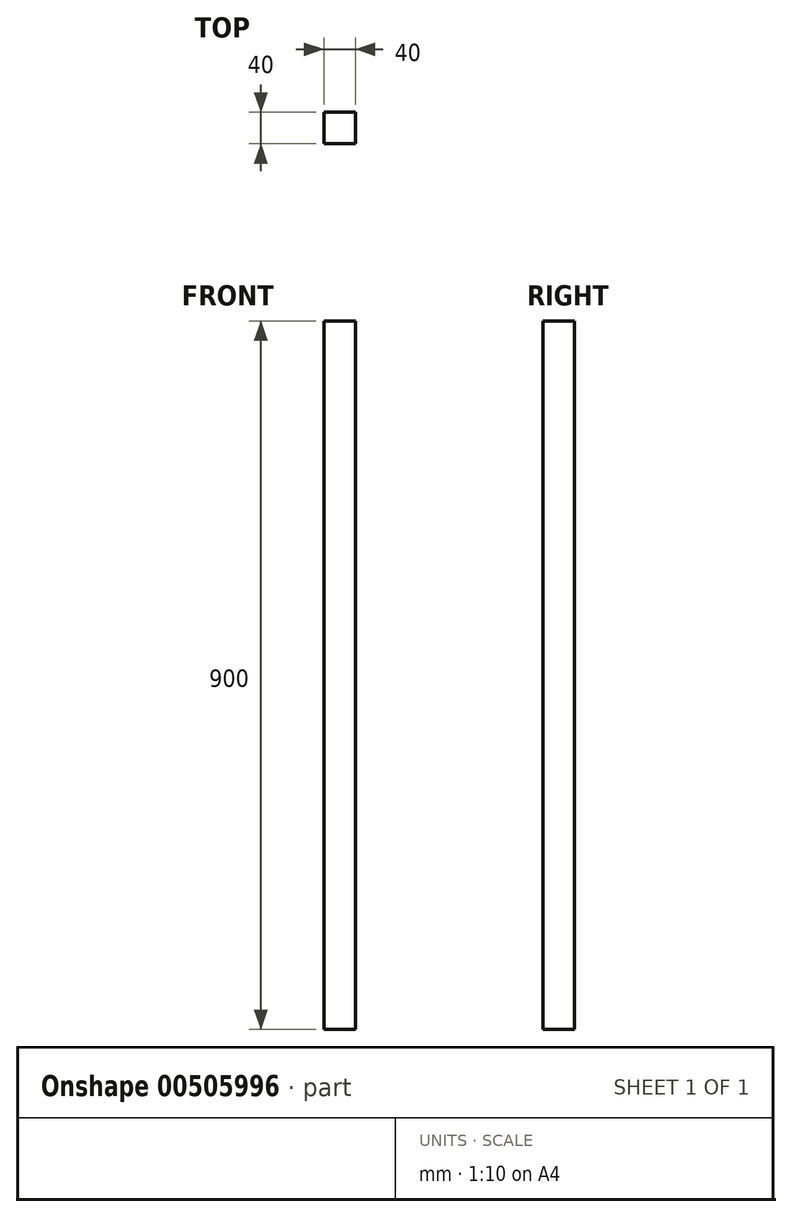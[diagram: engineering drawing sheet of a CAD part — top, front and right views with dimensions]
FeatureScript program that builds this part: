
annotation { "Feature Type Name" : "Feature", "Feature Type Description" : "" }
export const myFeature = defineFeature(function(context is Context, id is Id, definition is map)
    precondition{}
    {
        {
            var Q0;
            Q0=qCreatedBy(makeId("Top.planeOp"),FACE);
            var sketch = newSketch(context, id + "F0", { "sketchPlane" : qUnion([Q0])});
            skLineSegment(sketch, "E0.bottom", {"start": v(0, 0) * mm, "end": v(40, 0) * mm});
            skLineSegment(sketch, "E0.top", {"start": v(0, 40) * mm, "end": v(40, 40) * mm});
            skLineSegment(sketch, "E0.left", {"start": v(0, 0) * mm, "end": v(0, 40) * mm});
            skLineSegment(sketch, "E0.right", {"start": v(40, 0) * mm, "end": v(40, 40) * mm});
            skSolve(sketch);
        }
        {
            var Q0;
            Q0=makeQuery(id+"F0.imprint","IMPRINT",FACE,{"disambiguationData":[TD([[makeQuery(id+"F0.imprint","IMPRINT",EDGE,{"derivedFrom":sQuery(id+"F0.wireOp",EDGE,"E0.bottom")}),1.0]])]});
            extrude(context, id + "F1", {"entities" : qUnion([Q0]), "depth" : 900 * mm});
        }
        {
            var Q0;
            Q0=makeQuery(id+"F1.opExtrude","SWEPT_FACE",FACE,{"disambiguationData":[OSD([sQuery(id+"F0.wireOp",EDGE,"E0.right")])]});
            var sketch = newSketch(context, id + "F2", { "sketchPlane" : qUnion([Q0])});
            skCircle(sketch, "E1", {"center": v(17.78, 878.93) * mm, "radius": 3 * mm});
            skSolve(sketch);
        }
        {
            var Q0;
            Q0=makeQuery(id+"F2.imprint","IMPRINT",FACE,{"disambiguationData":[TD([[makeQuery(id+"F2.imprint","IMPRINT",EDGE,{"derivedFrom":sQuery(id+"F2.wireOp",EDGE,"E1")}),1.0]])]});
            extrude(context, id + "F3", {"entities" : qUnion([Q0]), "operationType" : NewBodyOperationType.REMOVE, "depth" : 15 * mm, "offsetDistance" : 25 * mm});
        }
    });
